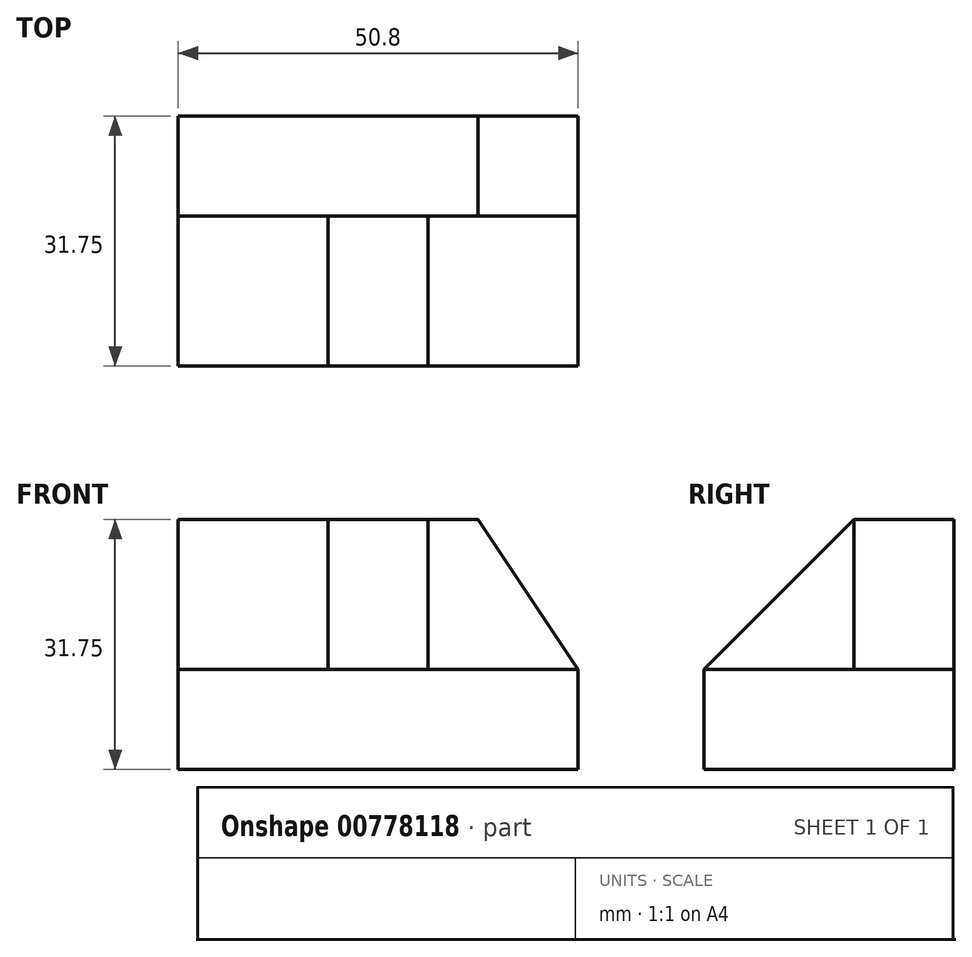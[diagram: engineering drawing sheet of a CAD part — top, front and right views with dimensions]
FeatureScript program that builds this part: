
annotation { "Feature Type Name" : "Feature", "Feature Type Description" : "" }
export const myFeature = defineFeature(function(context is Context, id is Id, definition is map)
    precondition{}
    {
        {
            var Q0;
            Q0=qCreatedBy(makeId("Front.planeOp"),FACE);
            var sketch = newSketch(context, id + "F0", { "sketchPlane" : qUnion([Q0])});
            skLineSegment(sketch, "E0", {"start": v(0, 0) * mm, "end": v(50.8, 0) * mm});
            skLineSegment(sketch, "E1", {"start": v(50.8, 0) * mm, "end": v(50.8, 31.75) * mm});
            skLineSegment(sketch, "E2", {"start": v(50.8, 31.75) * mm, "end": v(0, 31.75) * mm});
            skLineSegment(sketch, "E3", {"start": v(0, 31.75) * mm, "end": v(0, 0) * mm});
            skSolve(sketch);
        }
        {
            var Q0;
            Q0=makeQuery(id+"F0.imprint","IMPRINT",FACE,{"disambiguationData":[TD([[makeQuery(id+"F0.imprint","IMPRINT",EDGE,{"derivedFrom":sQuery(id+"F0.wireOp",EDGE,"E0")}),1.0]])]});
            extrude(context, id + "F1", {"entities" : qUnion([Q0]), "depth" : 31.75 * mm, "offsetDistance" : 25.4 * mm});
        }
        {
            var Q0;
            Q0=makeQuery(id+"F1.opExtrude","SWEPT_FACE",FACE,{"disambiguationData":[OSD([sQuery(id+"F0.wireOp",EDGE,"E1")])]});
            var sketch = newSketch(context, id + "F2", { "sketchPlane" : qUnion([Q0])});
            skLineSegment(sketch, "E4", {"start": v(-31.75, 0) * mm, "end": v(-31.75, 12.7) * mm});
            skLineSegment(sketch, "E5", {"start": v(-31.75, 12.7) * mm, "end": v(-12.7, 12.7) * mm});
            skLineSegment(sketch, "E6", {"start": v(-12.7, 12.7) * mm, "end": v(-12.7, 31.75) * mm});
            skSolve(sketch);
        }
        {
            var Q0;
            {var subQ0=sQuery(id+"F2.wireOp",EDGE,"E5");Q0=makeQuery(id+"F2.imprint","IMPRINT",FACE,{"disambiguationData":[TD([[makeQuery(id+"F2.imprint","IMPRINT",EDGE,{"derivedFrom":subQ0}),1.0]])]});}
            extrude(context, id + "F3", {"entities" : qUnion([Q0]), "operationType" : NewBodyOperationType.REMOVE, "oppositeDirection" : true, "depth" : 19.05 * mm, "offsetDistance" : 25.4 * mm});
        }
        {
            var Q0;
            Q0=makeQuery(id+"F1.opExtrude","SWEPT_FACE",FACE,{"disambiguationData":[OSD([sQuery(id+"F0.wireOp",EDGE,"E3")])]});
            var sketch = newSketch(context, id + "F4", { "sketchPlane" : qUnion([Q0])});
            skLineSegment(sketch, "E7", {"start": v(31.75, 0) * mm, "end": v(31.75, 12.7) * mm});
            skLineSegment(sketch, "E8", {"start": v(31.75, 12.7) * mm, "end": v(12.7, 12.7) * mm});
            skLineSegment(sketch, "E9", {"start": v(12.7, 12.7) * mm, "end": v(12.7, 31.75) * mm});
            skSolve(sketch);
        }
        {
            var Q0;
            {var subQ0=sQuery(id+"F4.wireOp",EDGE,"E8");Q0=makeQuery(id+"F4.imprint","IMPRINT",FACE,{"disambiguationData":[TD([[makeQuery(id+"F4.imprint","IMPRINT",EDGE,{"derivedFrom":subQ0}),-1.0]])]});}
            extrude(context, id + "F5", {"entities" : qUnion([Q0]), "operationType" : NewBodyOperationType.REMOVE, "oppositeDirection" : true, "depth" : 19.05 * mm, "offsetDistance" : 25.4 * mm});
        }
        {
            var Q0;
            Q0=makeQuery(id+"F3.boolean.opBoolean","COPY",FACE,{"derivedFrom":makeQuery(id+"F3.opExtrude","CAP_FACE",FACE,{"disambiguationData":[OSD([sQuery(id+"F0.wireOp",EDGE,"E1"),sQuery(id+"F0.wireOp",EDGE,"E2"),sQuery(id+"F2.wireOp",EDGE,"E5"),sQuery(id+"F2.wireOp",EDGE,"E6")])],"isStart":false})});
            var sketch = newSketch(context, id + "F6", { "sketchPlane" : qUnion([Q0])});
            skLineSegment(sketch, "E10", {"start": v(-12.7, 31.75) * mm, "end": v(-31.75, 12.7) * mm});
            skSolve(sketch);
        }
        {
            var Q0;
            Q0=makeQuery(id+"F6.imprint","IMPRINT",FACE,{"disambiguationData":[TD([[makeQuery(id+"F6.imprint","IMPRINT",EDGE,{"derivedFrom":sQuery(id+"F6.wireOp",EDGE,"E10")}),-1.0]])]});
            extrude(context, id + "F7", {"entities" : qUnion([Q0]), "operationType" : NewBodyOperationType.REMOVE, "oppositeDirection" : true, "depth" : 12.7 * mm, "offsetDistance" : 25.4 * mm});
        }
        {
            var Q0;
            Q0=makeQuery(id+"F3.boolean.opBoolean","COPY",FACE,{"derivedFrom":makeQuery(id+"F3.opExtrude","SWEPT_FACE",FACE,{"disambiguationData":[OSD([sQuery(id+"F2.wireOp",EDGE,"E6")])]})});
            var sketch = newSketch(context, id + "F8", { "sketchPlane" : qUnion([Q0])});
            skLineSegment(sketch, "E11", {"start": v(31.75, 31.75) * mm, "end": v(38.1, 31.75) * mm});
            skLineSegment(sketch, "E12", {"start": v(38.1, 31.75) * mm, "end": v(50.8, 12.7) * mm});
            skSolve(sketch);
        }
        {
            var Q0;
            {var subQ0=sQuery(id+"F8.wireOp",EDGE,"E12");Q0=makeQuery(id+"F8.imprint","IMPRINT",FACE,{"disambiguationData":[TD([[makeQuery(id+"F8.imprint","IMPRINT",EDGE,{"derivedFrom":subQ0}),1.0]])]});}
            extrude(context, id + "F9", {"entities" : qUnion([Q0]), "operationType" : NewBodyOperationType.REMOVE, "oppositeDirection" : true, "depth" : 12.7 * mm, "offsetDistance" : 25.4 * mm});
        }
    });
